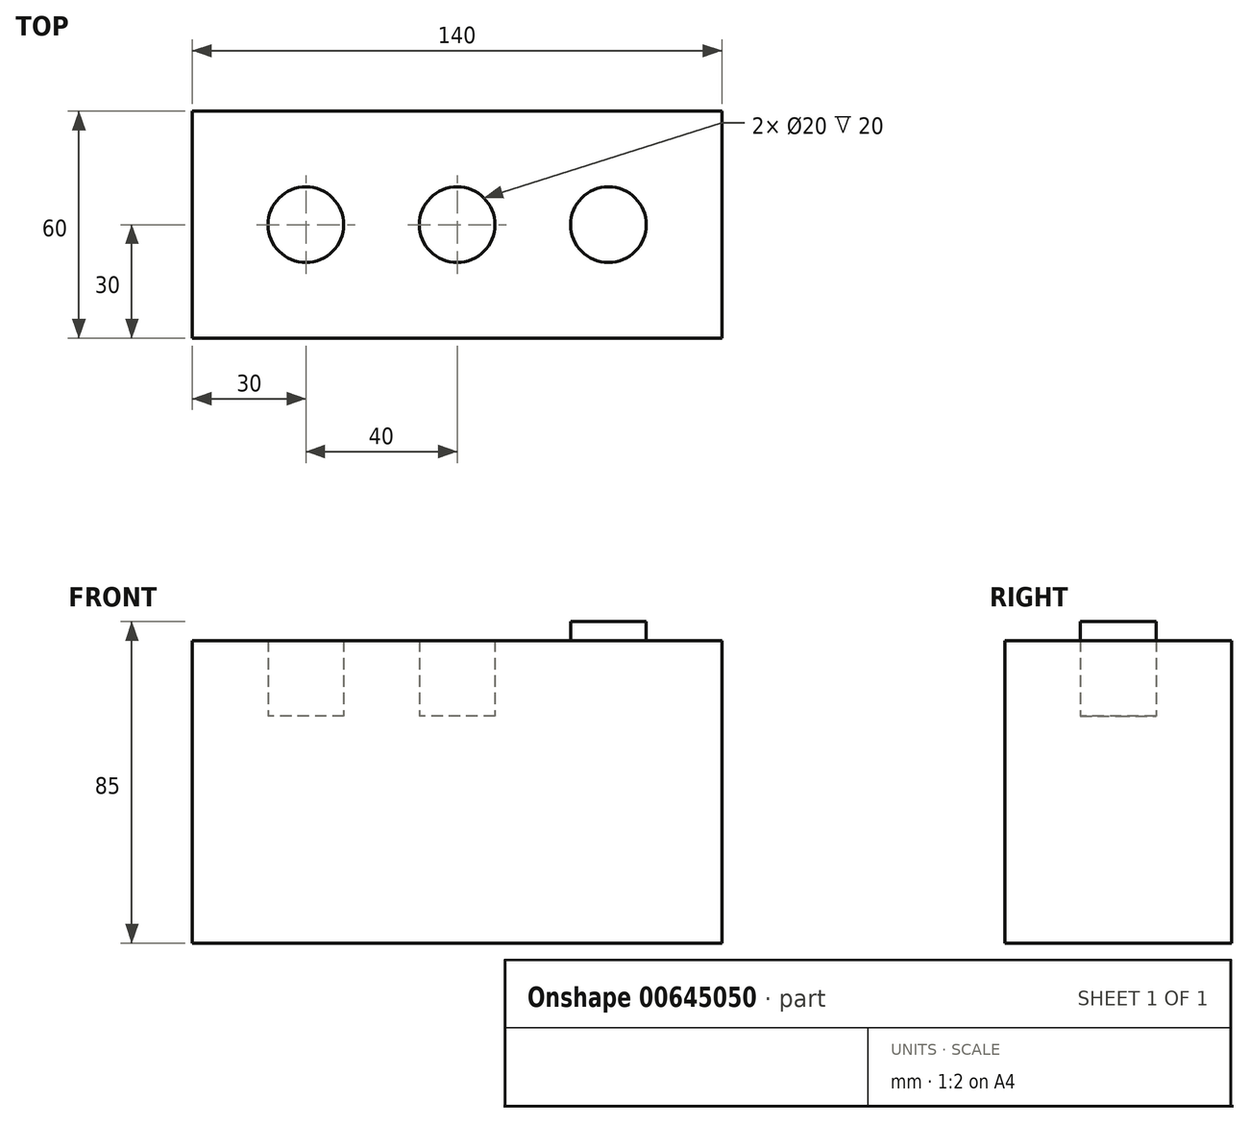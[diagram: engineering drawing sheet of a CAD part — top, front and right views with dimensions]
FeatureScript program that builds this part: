
annotation { "Feature Type Name" : "Feature", "Feature Type Description" : "" }
export const myFeature = defineFeature(function(context is Context, id is Id, definition is map)
    precondition{}
    {
        {
            var Q0;
            Q0=qCreatedBy(makeId("Top.planeOp"),FACE);
            var sketch = newSketch(context, id + "F0", { "sketchPlane" : qUnion([Q0])});
            skLineSegment(sketch, "E0.bottom", {"start": v(70, 30) * mm, "end": v(-70, 30) * mm});
            skLineSegment(sketch, "E0.top", {"start": v(70, -30) * mm, "end": v(-70, -30) * mm});
            skLineSegment(sketch, "E0.left", {"start": v(70, 30) * mm, "end": v(70, -30) * mm});
            skLineSegment(sketch, "E0.right", {"start": v(-70, 30) * mm, "end": v(-70, -30) * mm});
            skPoint(sketch, "E0.middle", {"position": v(0, 0) * mm});
            skSolve(sketch);
        }
        {
            var Q0;
            Q0 = qSketchRegion(id + "F0", true);
            extrude(context, id + "F1", {"entities" : qUnion([Q0]), "depth" : 60 * mm, "offsetDistance" : 25 * mm});
        }
        {
            var Q0;
            Q0=makeQuery(id+"F1.opExtrude","CAP_FACE",FACE,{"disambiguationData":[OSD([sQuery(id+"F0.wireOp",EDGE,"E0.bottom"),sQuery(id+"F0.wireOp",EDGE,"E0.top"),sQuery(id+"F0.wireOp",EDGE,"E0.left"),sQuery(id+"F0.wireOp",EDGE,"E0.right")])],"isStart":false});
            var sketch = newSketch(context, id + "F2", { "sketchPlane" : qUnion([Q0])});
            skCircle(sketch, "E1", {"center": v(-40, 0) * mm, "radius": 10 * mm});
            skSolve(sketch);
        }
        {
            var Q0;
            Q0=makeQuery(id+"F2.imprint","IMPRINT",FACE,{"disambiguationData":[TD([[makeQuery(id+"F2.imprint","IMPRINT",EDGE,{"derivedFrom":sQuery(id+"F2.wireOp",EDGE,"E1")}),-1.0]])]});
            var sketch = newSketch(context, id + "F3", { "sketchPlane" : qUnion([Q0])});
            skCircle(sketch, "E2", {"center": v(40, 0) * mm, "radius": 10 * mm});
            skSolve(sketch);
        }
        {
            var Q0;
            Q0=makeQuery(id+"F2.imprint","IMPRINT",FACE,{"disambiguationData":[TD([[makeQuery(id+"F2.imprint","IMPRINT",EDGE,{"derivedFrom":sQuery(id+"F2.wireOp",EDGE,"E1")}),-1.0]])]});
            var sketch = newSketch(context, id + "F4", { "sketchPlane" : qUnion([Q0])});
            skCircle(sketch, "E3", {"center": v(0, 0) * mm, "radius": 10 * mm});
            skSolve(sketch);
        }
        {
            var Q0;
            Q0=makeQuery(id+"F2.imprint","IMPRINT",FACE,{"disambiguationData":[TD([[makeQuery(id+"F2.imprint","IMPRINT",EDGE,{"derivedFrom":sQuery(id+"F2.wireOp",EDGE,"E1")}),-1.0]])]});
            extrude(context, id + "F5", {"entities" : qUnion([Q0]), "operationType" : NewBodyOperationType.ADD, "depth" : 20 * mm, "offsetDistance" : 25 * mm});
        }
        {
            var Q0;
            Q0=makeQuery(id+"F5.opExtrude","CAP_FACE",FACE,{"disambiguationData":[OSD([sQuery(id+"F0.wireOp",EDGE,"E0.bottom"),sQuery(id+"F0.wireOp",EDGE,"E0.top"),sQuery(id+"F0.wireOp",EDGE,"E0.left"),sQuery(id+"F0.wireOp",EDGE,"E0.right"),sQuery(id+"F2.wireOp",EDGE,"E1")])],"isStart":false});
            var sketch = newSketch(context, id + "F6", { "sketchPlane" : qUnion([Q0])});
            skSolve(sketch);
        }
        {
            var Q0;
            Q0=makeQuery(id+"F6.imprint","IMPRINT",FACE,{"disambiguationData":[TD([[makeQuery(id+"F6.imprint","IMPRINT",EDGE,{"derivedFrom":makeQuery(id+"F5.opExtrude","CAP_EDGE",EDGE,{"disambiguationData":[OSD([sQuery(id+"F2.wireOp",EDGE,"E1")])],"isStart":false})}),-1.0]])]});
            var sketch = newSketch(context, id + "F7", { "sketchPlane" : qUnion([Q0])});
            skSolve(sketch);
        }
        {
            var Q0;
            Q0 = qSketchRegion(id + "F7", true);
            var Q1;
            Q1 = qSketchRegion(id + "F4", true);
            extrude(context, id + "F8", {"entities" : qUnion([Q0, Q1]), "operationType" : NewBodyOperationType.REMOVE, "depth" : 500 * mm, "offsetDistance" : 25 * mm});
        }
        {
            var Q0;
            Q0 = qSketchRegion(id + "F3", true);
            extrude(context, id + "F9", {"entities" : qUnion([Q0]), "operationType" : NewBodyOperationType.ADD, "depth" : 25 * mm, "offsetDistance" : 25 * mm});
        }
    });
